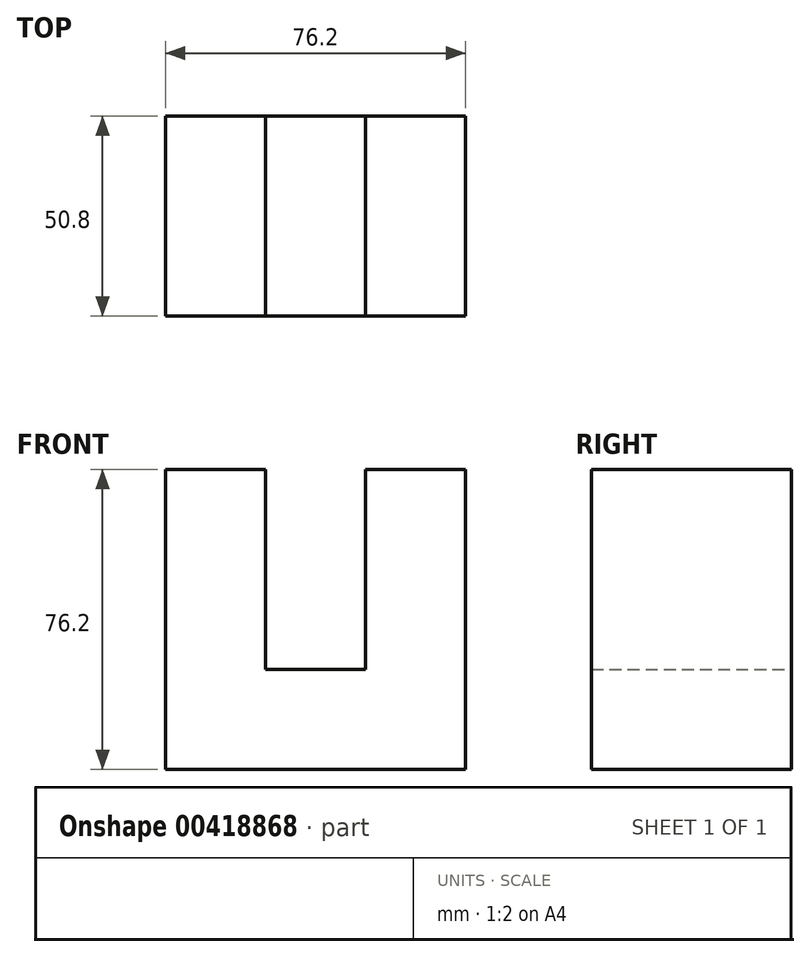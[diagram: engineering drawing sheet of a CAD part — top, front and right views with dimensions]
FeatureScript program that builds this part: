
annotation { "Feature Type Name" : "Feature", "Feature Type Description" : "" }
export const myFeature = defineFeature(function(context is Context, id is Id, definition is map)
    precondition{}
    {
        {
            var Q0;
            Q0=qCreatedBy(makeId("Front.planeOp"),FACE);
            var sketch = newSketch(context, id + "F0", { "sketchPlane" : qUnion([Q0])});
            skLineSegment(sketch, "E0", {"start": v(0, 0) * mm, "end": v(0, 76.2) * mm});
            skLineSegment(sketch, "E1", {"start": v(0, 0) * mm, "end": v(-76.2, 0) * mm});
            skLineSegment(sketch, "E2", {"start": v(-76.2, 0) * mm, "end": v(-76.2, 76.2) * mm});
            skLineSegment(sketch, "E3", {"start": v(-76.2, 76.2) * mm, "end": v(-50.8, 76.2) * mm});
            skLineSegment(sketch, "E4", {"start": v(-50.8, 76.2) * mm, "end": v(-50.8, 25.4) * mm});
            skLineSegment(sketch, "E5", {"start": v(-50.8, 25.4) * mm, "end": v(-25.4, 25.4) * mm});
            skLineSegment(sketch, "E6", {"start": v(-25.4, 25.4) * mm, "end": v(-25.4, 76.2) * mm});
            skLineSegment(sketch, "E7", {"start": v(0, 76.2) * mm, "end": v(-25.4, 76.2) * mm});
            skSolve(sketch);
        }
        {
            var Q0;
            Q0 = qSketchRegion(id + "F0", true);
            extrude(context, id + "F1", {"entities" : qUnion([Q0]), "depth" : 50.8 * mm});
        }
    });
